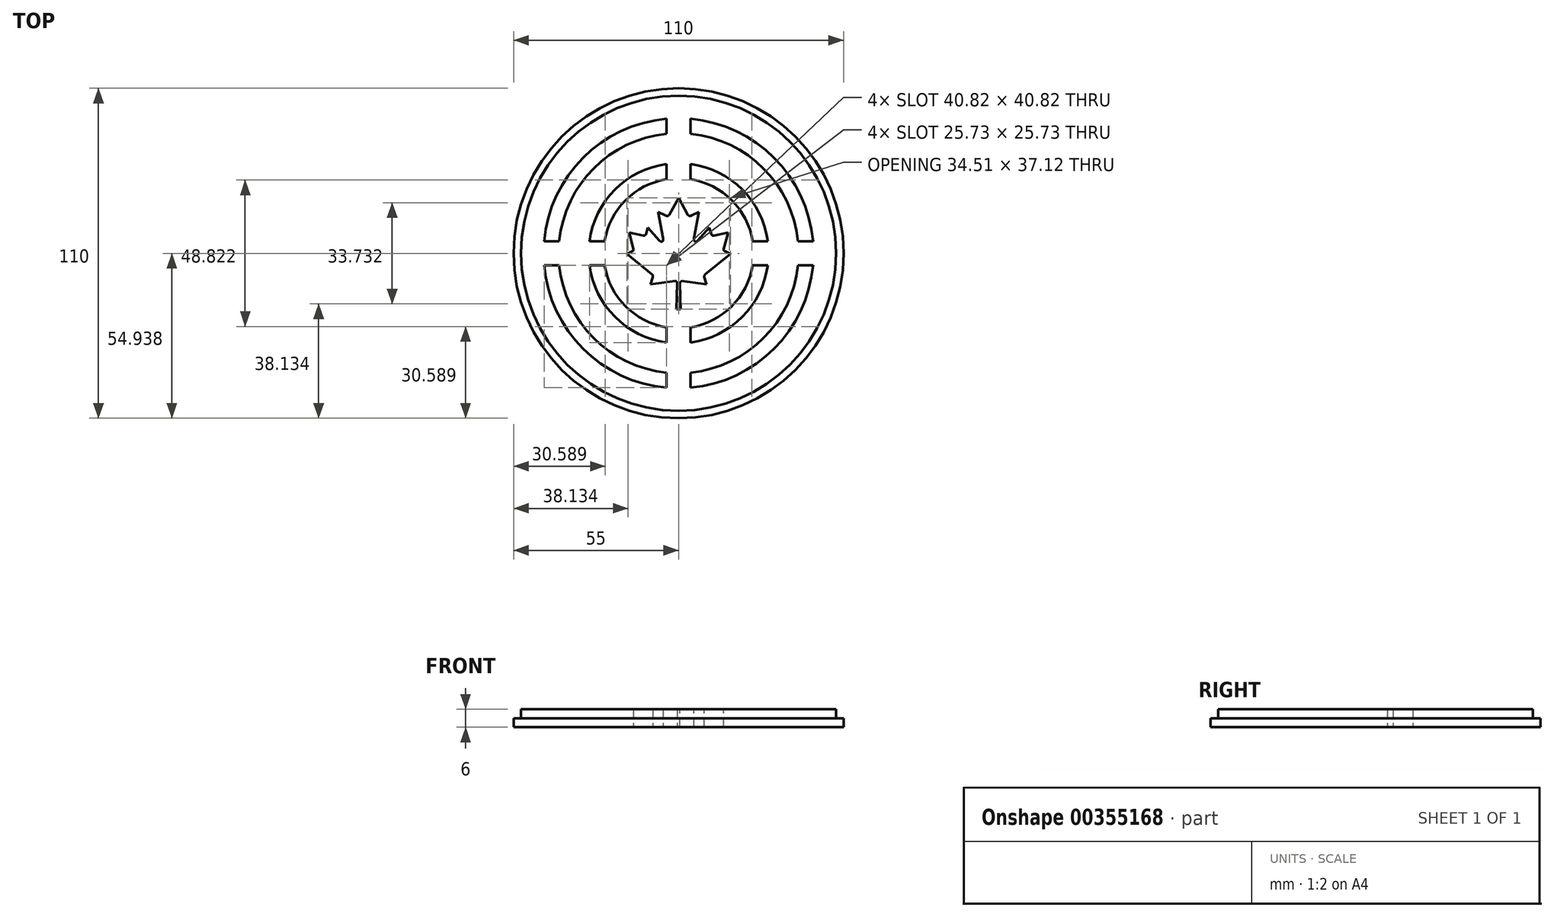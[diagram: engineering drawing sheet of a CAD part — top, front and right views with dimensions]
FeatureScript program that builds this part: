
annotation { "Feature Type Name" : "Feature", "Feature Type Description" : "" }
export const myFeature = defineFeature(function(context is Context, id is Id, definition is map)
    precondition{}
    {
        {
            var Q0;
            Q0=qCreatedBy(makeId("Top.planeOp"),FACE);
            var sketch = newSketch(context, id + "F0", { "sketchPlane" : qUnion([Q0])});
            skCircle(sketch, "E0", {"center": v(0, 0) * mm, "radius": 55 * mm});
            skCircle(sketch, "E1", {"center": v(0, 0) * mm, "radius": 52.5 * mm});
            skLineSegment(sketch, "E2", {"start": v(0, -18.62) * mm, "end": v(0.7, -18.62) * mm});
            skLineSegment(sketch, "E3", {"start": v(0.7, -18.62) * mm, "end": v(0.47, -9.95) * mm});
            skFitSpline(sketch, "E4", {"points": [v(0.47, -9.95) * mm, v(1.07, -9.26) * mm], "startDerivative": vector(-0.04, 0.33) * mm, "endDerivative": vector(1.23, 0.25) * mm});
            skLineSegment(sketch, "E5", {"start": v(1.07, -9.26) * mm, "end": v(9.34, -10.38) * mm});
            skLineSegment(sketch, "E6", {"start": v(9.34, -10.38) * mm, "end": v(8.6, -7.93) * mm});
            skFitSpline(sketch, "E7", {"points": [v(8.6, -7.93) * mm, v(8.82, -7.06) * mm], "startDerivative": vector(-0.03, 0.37) * mm, "endDerivative": vector(0.91, 1.07) * mm});
            skLineSegment(sketch, "E8", {"start": v(8.82, -7.06) * mm, "end": v(17.26, -0.2) * mm});
            skLineSegment(sketch, "E9", {"start": v(17.26, -0.2) * mm, "end": v(15.48, 0.65) * mm});
            skFitSpline(sketch, "E10", {"points": [v(15.48, 0.65) * mm, v(15.1, 0.9) * mm, v(15.05, 1.5) * mm], "startDerivative": vector(-1.16, 0.3) * mm, "endDerivative": vector(0.28, 1.91) * mm});
            skLineSegment(sketch, "E11", {"start": v(15.05, 1.5) * mm, "end": v(16.52, 6.91) * mm});
            skLineSegment(sketch, "E12", {"start": v(16.52, 6.91) * mm, "end": v(11.8, 5.92) * mm});
            skFitSpline(sketch, "E13", {"points": [v(11.8, 5.92) * mm, v(10.92, 6.3) * mm], "startDerivative": vector(-0.78, -0.2) * mm, "endDerivative": vector(-0.8, 1.35) * mm});
            skLineSegment(sketch, "E14", {"start": v(10.92, 6.3) * mm, "end": v(10.27, 8.58) * mm});
            skLineSegment(sketch, "E15", {"start": v(10.27, 8.58) * mm, "end": v(6.4, 4.23) * mm});
            skFitSpline(sketch, "E16", {"points": [v(6.4, 4.23) * mm, v(5.44, 3.95) * mm, v(5.13, 4.96) * mm], "startDerivative": vector(-1.88, -2.03) * mm, "endDerivative": vector(0.39, 2.99) * mm});
            skLineSegment(sketch, "E17", {"start": v(5.13, 4.96) * mm, "end": v(6.8, 13.81) * mm});
            skLineSegment(sketch, "E18", {"start": v(6.8, 13.81) * mm, "end": v(4.39, 12.58) * mm});
            skFitSpline(sketch, "E19", {"points": [v(4.39, 12.58) * mm, v(3.13, 12.8) * mm], "startDerivative": vector(-1.71, -0.55) * mm, "endDerivative": vector(-1.44, 1.49) * mm});
            skLineSegment(sketch, "E20", {"start": v(3.13, 12.8) * mm, "end": v(0, 18.5) * mm});
            skLineSegment(sketch, "E21.MirrorCS", {"start": v(-3.13, 12.8) * mm, "end": v(0, 18.5) * mm});
            skFitSpline(sketch, "E22.MirrorCS", {"points": [v(-4.39, 12.58) * mm, v(-3.13, 12.8) * mm], "startDerivative": vector(1.71, -0.55) * mm, "endDerivative": vector(1.44, 1.49) * mm});
            skLineSegment(sketch, "E23.MirrorCS", {"start": v(-6.8, 13.81) * mm, "end": v(-4.39, 12.58) * mm});
            skLineSegment(sketch, "E24.MirrorCS", {"start": v(-5.13, 4.96) * mm, "end": v(-6.8, 13.81) * mm});
            skFitSpline(sketch, "E25.MirrorCS", {"points": [v(-6.4, 4.23) * mm, v(-5.44, 3.95) * mm, v(-5.13, 4.96) * mm], "startDerivative": vector(1.88, -2.03) * mm, "endDerivative": vector(-0.39, 2.99) * mm});
            skLineSegment(sketch, "E26.MirrorCS", {"start": v(-10.27, 8.58) * mm, "end": v(-6.4, 4.23) * mm});
            skLineSegment(sketch, "E27.MirrorCS", {"start": v(-10.92, 6.3) * mm, "end": v(-10.27, 8.58) * mm});
            skFitSpline(sketch, "E28.MirrorCS", {"points": [v(-11.8, 5.92) * mm, v(-10.92, 6.3) * mm], "startDerivative": vector(0.78, -0.2) * mm, "endDerivative": vector(0.8, 1.35) * mm});
            skLineSegment(sketch, "E29.MirrorCS", {"start": v(-16.52, 6.91) * mm, "end": v(-11.8, 5.92) * mm});
            skLineSegment(sketch, "E30.MirrorCS", {"start": v(-15.05, 1.5) * mm, "end": v(-16.52, 6.91) * mm});
            skFitSpline(sketch, "E31.MirrorCS", {"points": [v(-15.48, 0.65) * mm, v(-15.1, 0.9) * mm, v(-15.05, 1.5) * mm], "startDerivative": vector(1.16, 0.3) * mm, "endDerivative": vector(-0.28, 1.91) * mm});
            skLineSegment(sketch, "E32.MirrorCS", {"start": v(-17.26, -0.2) * mm, "end": v(-15.48, 0.65) * mm});
            skLineSegment(sketch, "E33.MirrorCS", {"start": v(-8.82, -7.06) * mm, "end": v(-17.26, -0.2) * mm});
            skFitSpline(sketch, "E34.MirrorCS", {"points": [v(-8.6, -7.93) * mm, v(-8.82, -7.06) * mm], "startDerivative": vector(0.03, 0.37) * mm, "endDerivative": vector(-0.91, 1.07) * mm});
            skLineSegment(sketch, "E35.MirrorCS", {"start": v(-9.34, -10.38) * mm, "end": v(-8.6, -7.93) * mm});
            skLineSegment(sketch, "E36.MirrorCS", {"start": v(-1.07, -9.26) * mm, "end": v(-9.34, -10.38) * mm});
            skFitSpline(sketch, "E37.MirrorCS", {"points": [v(-0.47, -9.95) * mm, v(-1.07, -9.26) * mm], "startDerivative": vector(0.04, 0.33) * mm, "endDerivative": vector(-1.23, 0.25) * mm});
            skLineSegment(sketch, "E38.MirrorCS", {"start": v(-0.7, -18.62) * mm, "end": v(-0.47, -9.95) * mm});
            skLineSegment(sketch, "E39.MirrorCS", {"start": v(0, -18.62) * mm, "end": v(-0.7, -18.62) * mm});
            skArc(sketch, "E40", {"start": v(-4, 24.68) * mm, "mid": v(-17.68, 17.68) * mm, "end": v(-24.68, 4) * mm});
            skArc(sketch, "E41", {"start": v(-4, 29.73) * mm, "mid": v(-21.21, 21.21) * mm, "end": v(-29.73, 4) * mm});
            skArc(sketch, "E42", {"start": v(-4, 39.8) * mm, "mid": v(-28.28, 28.28) * mm, "end": v(-39.8, 4) * mm});
            skArc(sketch, "E43", {"start": v(-4, 44.82) * mm, "mid": v(-31.82, 31.82) * mm, "end": v(-44.82, 4) * mm});
            skLineSegment(sketch, "E44.left", {"start": v(4, 44.82) * mm, "end": v(4, 39.8) * mm});
            skLineSegment(sketch, "E44.right", {"start": v(-4, 44.82) * mm, "end": v(-4, 39.8) * mm});
            skPoint(sketch, "E44.middle", {"position": v(0, 35.12) * mm});
            skLineSegment(sketch, "E45.bottom", {"start": v(44.82, 4) * mm, "end": v(39.8, 4) * mm});
            skLineSegment(sketch, "E45.top", {"start": v(44.82, -4) * mm, "end": v(39.8, -4) * mm});
            skPoint(sketch, "E45.middle", {"position": v(35.25, 0) * mm});
            skLineSegment(sketch, "E46.MirrorCS", {"start": v(4, -44.82) * mm, "end": v(4, -39.8) * mm});
            skLineSegment(sketch, "E47.MirrorCS", {"start": v(-4, -44.82) * mm, "end": v(-4, -39.8) * mm});
            skLineSegment(sketch, "E48.MirrorCS", {"start": v(-44.82, -4) * mm, "end": v(-39.8, -4) * mm});
            skLineSegment(sketch, "E49.MirrorCS", {"start": v(-44.82, 4) * mm, "end": v(-39.8, 4) * mm});
            skLineSegment(sketch, "E50.trimOffspring", {"start": v(-29.73, -4) * mm, "end": v(-24.68, -4) * mm});
            skLineSegment(sketch, "E51.trimOffspring", {"start": v(-29.73, 4) * mm, "end": v(-24.68, 4) * mm});
            skPoint(sketch, "E52.orphan", {"position": v(-21.48, 4) * mm});
            skPoint(sketch, "E53.orphan", {"position": v(-21.48, -4) * mm});
            skPoint(sketch, "E54.orphan", {"position": v(-49.02, -4) * mm});
            skPoint(sketch, "E55.orphan", {"position": v(-49.02, 4) * mm});
            skLineSegment(sketch, "E56.trimOffspring", {"start": v(-4, -29.73) * mm, "end": v(-4, -24.68) * mm});
            skLineSegment(sketch, "E57.trimOffspring", {"start": v(4, -29.73) * mm, "end": v(4, -24.68) * mm});
            skPoint(sketch, "E58.MirrorCS.end.orphan", {"position": v(-4, -22.35) * mm});
            skPoint(sketch, "E58.MirrorCS.start.orphan", {"position": v(4, -22.35) * mm});
            skPoint(sketch, "E59.orphan", {"position": v(-4, -47.9) * mm});
            skPoint(sketch, "E60.orphan", {"position": v(4, -47.9) * mm});
            skLineSegment(sketch, "E61.trimOffspring", {"start": v(29.73, -4) * mm, "end": v(24.68, -4) * mm});
            skLineSegment(sketch, "E62.trimOffspring", {"start": v(29.73, 4) * mm, "end": v(24.68, 4) * mm});
            skPoint(sketch, "E63.orphan", {"position": v(21.48, -4) * mm});
            skPoint(sketch, "E64.orphan", {"position": v(21.48, 4) * mm});
            skPoint(sketch, "E45.left.end.orphan", {"position": v(49.02, -4) * mm});
            skPoint(sketch, "E65.orphan", {"position": v(49.02, 4) * mm});
            skLineSegment(sketch, "E66.trimOffspring", {"start": v(4, 29.73) * mm, "end": v(4, 24.68) * mm});
            skPoint(sketch, "E67.orphan", {"position": v(4, 22.35) * mm});
            skPoint(sketch, "E68.orphan", {"position": v(-4, 22.35) * mm});
            skLineSegment(sketch, "E69.trimOffspring", {"start": v(-4, 29.73) * mm, "end": v(-4, 24.68) * mm});
            skPoint(sketch, "E44.bottom.end.orphan", {"position": v(-4, 47.9) * mm});
            skPoint(sketch, "E70.orphan", {"position": v(4, 47.9) * mm});
            skArc(sketch, "E71.trimOffspring", {"start": v(-24.68, -4) * mm, "mid": v(-17.68, -17.68) * mm, "end": v(-4, -24.68) * mm});
            skArc(sketch, "E72.trimOffspring", {"start": v(-29.73, -4) * mm, "mid": v(-21.21, -21.21) * mm, "end": v(-4, -29.73) * mm});
            skArc(sketch, "E73.trimOffspring", {"start": v(-39.8, -4) * mm, "mid": v(-28.28, -28.28) * mm, "end": v(-4, -39.8) * mm});
            skArc(sketch, "E74.trimOffspring", {"start": v(-44.82, -4) * mm, "mid": v(-31.82, -31.82) * mm, "end": v(-4, -44.82) * mm});
            skArc(sketch, "E75.trimOffspring", {"start": v(4, -24.68) * mm, "mid": v(17.68, -17.68) * mm, "end": v(24.68, -4) * mm});
            skArc(sketch, "E76.trimOffspring", {"start": v(4, -29.73) * mm, "mid": v(21.21, -21.21) * mm, "end": v(29.73, -4) * mm});
            skArc(sketch, "E77.trimOffspring", {"start": v(4, -39.8) * mm, "mid": v(28.28, -28.28) * mm, "end": v(39.8, -4) * mm});
            skArc(sketch, "E78.trimOffspring", {"start": v(4, -44.82) * mm, "mid": v(31.82, -31.82) * mm, "end": v(44.82, -4) * mm});
            skArc(sketch, "E79.trimOffspring", {"start": v(24.68, 4) * mm, "mid": v(17.68, 17.68) * mm, "end": v(4, 24.68) * mm});
            skArc(sketch, "E80.trimOffspring", {"start": v(29.73, 4) * mm, "mid": v(21.21, 21.21) * mm, "end": v(4, 29.73) * mm});
            skArc(sketch, "E81.trimOffspring", {"start": v(39.8, 4) * mm, "mid": v(28.28, 28.28) * mm, "end": v(4, 39.8) * mm});
            skArc(sketch, "E82.trimOffspring", {"start": v(44.82, 4) * mm, "mid": v(31.82, 31.82) * mm, "end": v(4, 44.82) * mm});
            skSolve(sketch);
        }
        {
            var Q0;
            Q0=makeQuery(id+"F0.imprint","IMPRINT",FACE,{"disambiguationData":[TD([[makeQuery(id+"F0.imprint","IMPRINT",EDGE,{"derivedFrom":sQuery(id+"F0.wireOp",EDGE,"E1")}),1.0]])]});
            var Q1;
            Q1=makeQuery(id+"F0.imprint","IMPRINT",FACE,{"disambiguationData":[TD([[makeQuery(id+"F0.imprint","IMPRINT",EDGE,{"derivedFrom":sQuery(id+"F0.wireOp",EDGE,"E0")}),1.0]])]});
            extrude(context, id + "F1", {"entities" : qUnion([Q0, Q1]), "oppositeDirection" : true, "depth" : 6 * mm});
        }
        {
            var Q0;
            Q0=makeQuery(id+"F0.imprint","IMPRINT",FACE,{"disambiguationData":[TD([[makeQuery(id+"F0.imprint","IMPRINT",EDGE,{"derivedFrom":sQuery(id+"F0.wireOp",EDGE,"E0")}),1.0]])]});
            extrude(context, id + "F2", {"entities" : qUnion([Q0]), "operationType" : NewBodyOperationType.REMOVE, "oppositeDirection" : true, "depth" : 3 * mm});
        }
    });
